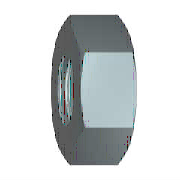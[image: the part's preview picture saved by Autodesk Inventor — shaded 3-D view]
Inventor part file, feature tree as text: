
AUTODESK INVENTOR PART (.ipt)
format: ipt  version: 2016 (Build 200138000, 138)  size: 161,280 bytes
history: native  units: mm (DEFAULTED — no unit token found)
features: sketch x3, chamfer x1, hole x1, other x1, plane x1
ambient origin geometry x7: Origin, YZ Plane, XZ Plane, X Axis, Y Axis, Z Axis, Center Point
bodies: Solid1 (feature_tree), Body (feature_tree)
feature tree (7):
  chamfer  "Chamfer1"  Angle=30.0deg  [1 undecoded]
  hole  "Thread"  [1 undecoded]
  other  "Work Axis1"
  plane  "Work Plane1"
  sketch  "Sketch1"  dims[d0=19.629909mm]
  sketch  "Sketch2"  dims[d1=8.0mm]
  sketch  "Sketch3"  dims[d2=0.0mm d3=30.0deg d4=30.0deg d5=14.5mm d6=14.5mm d7=90.0deg d25=8.376mm d26=6.0mm d27=4.0mm d28=2.0mm d29=14.3117mm d30=8.0mm d31=20.594885mm d8=0.811899mm d9=30.0deg d10=0.811899mm d11=30.0deg d13=0.0mm d14=0.0mm d39=0.0mm d40=0.811899mm d41=0.811899mm d42=0.0mm]
note: 2 required parameter values undecoded (feature->parameter linkage not recoverable at this tier; creation-order binding heuristic only, values carry confidence <= 0.55)
